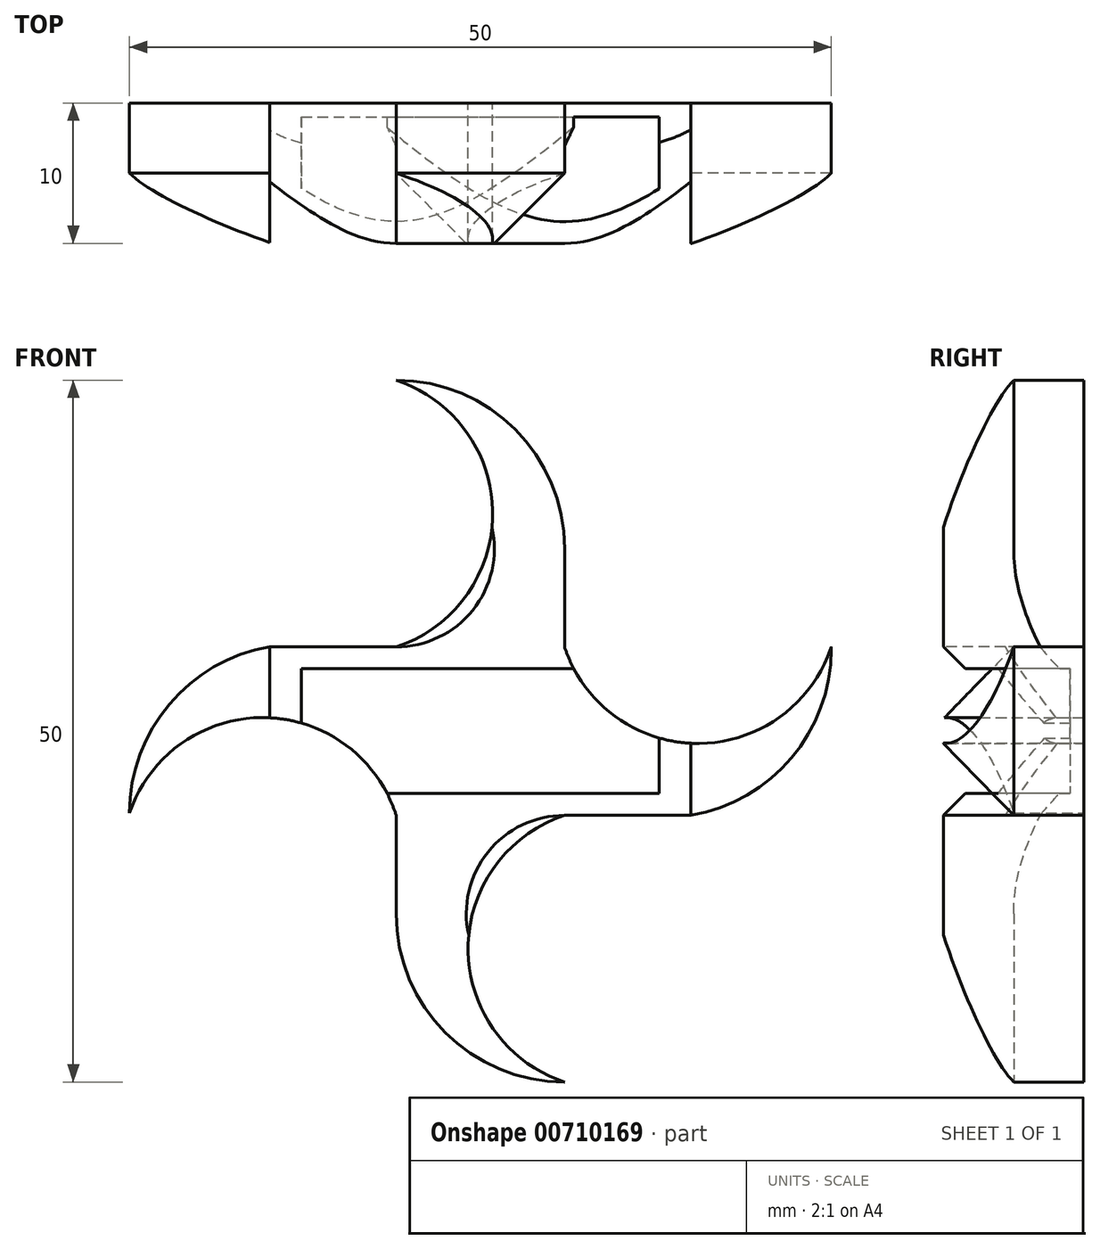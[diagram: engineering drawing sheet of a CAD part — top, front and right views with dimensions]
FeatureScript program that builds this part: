
annotation { "Feature Type Name" : "Feature", "Feature Type Description" : "" }
export const myFeature = defineFeature(function(context is Context, id is Id, definition is map)
    precondition{}
    {
        {
            var Q0;
            Q0=qCreatedBy(makeId("Top.planeOp"),FACE);
            var sketch = newSketch(context, id + "F0", { "sketchPlane" : qUnion([Q0])});
            skLineSegment(sketch, "E0", {"start": v(0, 0) * mm, "end": v(25.5, 0) * mm});
            skLineSegment(sketch, "E1", {"start": v(25.5, 0) * mm, "end": v(25.5, 8.9) * mm});
            skLineSegment(sketch, "E2", {"start": v(25.5, 8.9) * mm, "end": v(0, 8.9) * mm});
            skLineSegment(sketch, "E3", {"start": v(0, 8.9) * mm, "end": v(0, 0) * mm});
            skSolve(sketch);
        }
        {
            var Q0;
            Q0=makeQuery(id+"F0.imprint","IMPRINT",FACE,{"disambiguationData":[TD([[makeQuery(id+"F0.imprint","IMPRINT",EDGE,{"derivedFrom":sQuery(id+"F0.wireOp",EDGE,"E0")}),1.0]])]});
            extrude(context, id + "F1", {"entities" : qUnion([Q0]), "depth" : 8.9 * mm, "offsetDistance" : 25 * mm});
        }
        {
            var Q0;
            Q0=makeQuery(id+"F1.opExtrude","SWEPT_FACE",FACE,{"disambiguationData":[OSD([sQuery(id+"F0.wireOp",EDGE,"E0")])]});
            var sketch = newSketch(context, id + "F2", { "sketchPlane" : qUnion([Q0])});
            skLineSegment(sketch, "E4.bottom", {"start": v(-2.25, 10.45) * mm, "end": v(27.75, 10.45) * mm});
            skLineSegment(sketch, "E4.top", {"start": v(-2.25, -1.55) * mm, "end": v(27.75, -1.55) * mm});
            skLineSegment(sketch, "E4.left", {"start": v(-2.25, 10.45) * mm, "end": v(-2.25, -1.55) * mm});
            skLineSegment(sketch, "E4.right", {"start": v(27.75, 10.45) * mm, "end": v(27.75, -1.55) * mm});
            skPoint(sketch, "E4.middle", {"position": v(12.75, 4.45) * mm});
            skSolve(sketch);
        }
        {
            var Q0;
            {var subQ0=sQuery(id+"F0.wireOp",EDGE,"E0");Q0=makeQuery(id+"F2.imprint","IMPRINT",FACE,{"disambiguationData":[TD([[makeQuery(id+"F2.imprint","IMPRINT",EDGE,{"derivedFrom":makeQuery(id+"F1.opExtrude","CAP_EDGE",EDGE,{"disambiguationData":[OSD([subQ0])],"isStart":true})}),1.0]])]});}
            var Q1;
            Q1=makeQuery(id+"F2.imprint","IMPRINT",FACE,{"disambiguationData":[TD([[makeQuery(id+"F2.imprint","IMPRINT",EDGE,{"derivedFrom":sQuery(id+"F2.wireOp",EDGE,"E4.bottom")}),-1.0]])]});
            extrude(context, id + "F3", {"entities" : qUnion([Q0, Q1]), "oppositeDirection" : true, "depth" : 10 * mm, "offsetDistance" : 25 * mm});
        }
        {
            var Q0;
            Q0=makeQuery(id+"F1.opExtrude","SWEPT_FACE",FACE,{"disambiguationData":[OSD([sQuery(id+"F0.wireOp",EDGE,"E0")])]});
            extrude(context, id + "F4", {"entities" : qUnion([Q0]), "operationType" : NewBodyOperationType.REMOVE, "oppositeDirection" : true, "depth" : 9 * mm, "offsetDistance" : 25 * mm});
        }
        {
            var Q0;
            Q0=makeQuery(id+"F3.opExtrude","SWEPT_FACE",FACE,{"disambiguationData":[OSD([sQuery(id+"F2.wireOp",EDGE,"E4.left")])]});
            extrude(context, id + "F5", {"entities" : qUnion([Q0]), "depth" : 10 * mm, "offsetDistance" : 25 * mm});
        }
        {
            var Q0;
            Q0=makeQuery(id+"F3.opExtrude","SWEPT_FACE",FACE,{"disambiguationData":[OSD([sQuery(id+"F2.wireOp",EDGE,"E4.right")])]});
            extrude(context, id + "F6", {"entities" : qUnion([Q0]), "depth" : 10 * mm, "offsetDistance" : 25 * mm});
        }
        {
            var Q0;
            Q0=makeQuery(id+"F3.opExtrude","SWEPT_FACE",FACE,{"disambiguationData":[OSD([sQuery(id+"F2.wireOp",EDGE,"E4.bottom")])]});
            var sketch = newSketch(context, id + "F7", { "sketchPlane" : qUnion([Q0])});
            skLineSegment(sketch, "E5", {"start": v(12.75, 0) * mm, "end": v(18.75, 0) * mm});
            skLineSegment(sketch, "E6", {"start": v(18.75, 0) * mm, "end": v(18.75, 10) * mm});
            skLineSegment(sketch, "E7", {"start": v(18.75, 10) * mm, "end": v(12.75, 10) * mm});
            skLineSegment(sketch, "E8", {"start": v(12.75, 10) * mm, "end": v(6.75, 10) * mm});
            skLineSegment(sketch, "E9", {"start": v(6.75, 10) * mm, "end": v(6.75, 0) * mm});
            skLineSegment(sketch, "E10", {"start": v(12.75, 0) * mm, "end": v(6.75, 0) * mm});
            skSolve(sketch);
        }
        {
            var Q0;
            Q0=makeQuery(id+"F7.imprint","IMPRINT",FACE,{"disambiguationData":[TD([[makeQuery(id+"F7.imprint","IMPRINT",EDGE,{"derivedFrom":sQuery(id+"F7.wireOp",EDGE,"E5")}),1.0]])]});
            extrude(context, id + "F8", {"entities" : qUnion([Q0]), "operationType" : NewBodyOperationType.ADD, "depth" : 19 * mm, "offsetDistance" : 25 * mm});
        }
        {
            var Q0;
            Q0=makeQuery(id+"F3.opExtrude","SWEPT_FACE",FACE,{"disambiguationData":[OSD([sQuery(id+"F2.wireOp",EDGE,"E4.top")])]});
            var sketch = newSketch(context, id + "F9", { "sketchPlane" : qUnion([Q0])});
            skLineSegment(sketch, "E11", {"start": v(12.75, -10) * mm, "end": v(18.75, -10) * mm});
            skLineSegment(sketch, "E12", {"start": v(18.75, -10) * mm, "end": v(18.75, 0) * mm});
            skLineSegment(sketch, "E13", {"start": v(12.75, 0) * mm, "end": v(18.75, 0) * mm});
            skLineSegment(sketch, "E14", {"start": v(12.75, 0) * mm, "end": v(6.75, 0) * mm});
            skLineSegment(sketch, "E15", {"start": v(6.75, 0) * mm, "end": v(6.75, -10) * mm});
            skLineSegment(sketch, "E16", {"start": v(6.75, -10) * mm, "end": v(12.75, -10) * mm});
            skSolve(sketch);
        }
        {
            var Q0;
            Q0=makeQuery(id+"F9.imprint","IMPRINT",FACE,{"disambiguationData":[TD([[makeQuery(id+"F9.imprint","IMPRINT",EDGE,{"derivedFrom":sQuery(id+"F9.wireOp",EDGE,"E11")}),1.0]])]});
            extrude(context, id + "F10", {"entities" : qUnion([Q0]), "operationType" : NewBodyOperationType.ADD, "depth" : 19 * mm, "offsetDistance" : 25 * mm});
        }
        {
            var Q0;
            Q0=makeQuery(id+"F10.opExtrude","CAP_EDGE",EDGE,{"disambiguationData":[OSD([sQuery(id+"F9.wireOp",EDGE,"E15")])],"isStart":false});
            var Q1;
            Q1=makeQuery(id+"F5.opExtrude","CAP_EDGE",EDGE,{"disambiguationData":[OSD([sQuery(id+"F2.wireOp",EDGE,"E4.bottom"),sQuery(id+"F2.wireOp",EDGE,"E4.left")])],"isStart":false});
            var Q2;
            Q2=makeQuery(id+"F8.opExtrude","CAP_EDGE",EDGE,{"disambiguationData":[OSD([sQuery(id+"F7.wireOp",EDGE,"E6")])],"isStart":false});
            var Q3;
            Q3=makeQuery(id+"F6.opExtrude","CAP_EDGE",EDGE,{"disambiguationData":[OSD([sQuery(id+"F2.wireOp",EDGE,"E4.top"),sQuery(id+"F2.wireOp",EDGE,"E4.right")])],"isStart":false});
            fillet(context, id + "F11", {"entities" : qUnion([Q0, Q1, Q2, Q3]), "radius" : 12 * mm, "tangentPropagation" : true, "allowEdgeOverflow" : false});
        }
        {
            var Q0;
            Q0=makeQuery(id+"F10.boolean.opBoolean","MERGE",FACE,{"derivedFrom":[makeQuery(id+"F8.boolean.opBoolean","MERGE",FACE,{"derivedFrom":[makeQuery(id+"F3.opExtrude","CAP_FACE",FACE,{"disambiguationData":[OSD([sQuery(id+"F2.wireOp",EDGE,"E4.bottom"),sQuery(id+"F2.wireOp",EDGE,"E4.top"),sQuery(id+"F2.wireOp",EDGE,"E4.left"),sQuery(id+"F2.wireOp",EDGE,"E4.right")])],"isStart":false}),makeQuery(id+"F8.opExtrude","SWEPT_FACE",FACE,{"disambiguationData":[OSD([sQuery(id+"F7.wireOp",EDGE,"E7"),sQuery(id+"F7.wireOp",EDGE,"E8")])]})]}),makeQuery(id+"F10.opExtrude","SWEPT_FACE",FACE,{"disambiguationData":[OSD([sQuery(id+"F9.wireOp",EDGE,"E11"),sQuery(id+"F9.wireOp",EDGE,"E16")])]})]});
            var sketch = newSketch(context, id + "F12", { "sketchPlane" : qUnion([Q0])});
            skPoint(sketch, "E17.0", {"position": v(-12.75, 10.45) * mm});
            skLineSegment(sketch, "E18", {"start": v(-18.75, 10.45) * mm, "end": v(-18.75, -1.55) * mm});
            skLineSegment(sketch, "E19", {"start": v(-18.75, -1.55) * mm, "end": v(-6.75, -1.55) * mm});
            skLineSegment(sketch, "E20", {"start": v(-6.75, -1.55) * mm, "end": v(-6.75, 10.45) * mm});
            skLineSegment(sketch, "E21", {"start": v(-6.75, 10.45) * mm, "end": v(-18.75, 10.45) * mm});
            skLineSegment(sketch, "E22.0.0", {"start": v(12.25, -1.55) * mm, "end": v(12.25, -1.38) * mm});
            skArc(sketch, "E22.0.1", {"start": v(12.25, -1.38) * mm, "mid": v(9.42, 6.36) * mm, "end": v(2.25, 10.45) * mm});
            skLineSegment(sketch, "E22.0.2", {"start": v(2.25, 10.45) * mm, "end": v(2.25, -1.55) * mm});
            skLineSegment(sketch, "E22.0.3", {"start": v(2.25, -1.55) * mm, "end": v(12.25, -1.55) * mm});
            skLineSegment(sketch, "E23.0.0", {"start": v(-37.75, 10.45) * mm, "end": v(-37.75, 10.28) * mm});
            skArc(sketch, "E23.0.1", {"start": v(-37.75, 10.28) * mm, "mid": v(-34.92, 2.54) * mm, "end": v(-27.75, -1.55) * mm});
            skLineSegment(sketch, "E23.0.2", {"start": v(-27.75, -1.55) * mm, "end": v(-27.75, 10.45) * mm});
            skLineSegment(sketch, "E23.0.3", {"start": v(-27.75, 10.45) * mm, "end": v(-37.75, 10.45) * mm});
            skLineSegment(sketch, "E24.0.0", {"start": v(-18.75, -1.55) * mm, "end": v(-18.75, -20.55) * mm});
            skArc(sketch, "E24.0.1", {"start": v(-18.75, -20.55) * mm, "mid": v(-10.26, -17.04) * mm, "end": v(-6.75, -8.55) * mm});
            skLineSegment(sketch, "E24.0.2", {"start": v(-6.75, -8.55) * mm, "end": v(-6.75, -1.55) * mm});
            skLineSegment(sketch, "E24.0.3", {"start": v(-6.75, -1.55) * mm, "end": v(2.25, -1.55) * mm});
            skLineSegment(sketch, "E24.0.4", {"start": v(2.25, -1.55) * mm, "end": v(2.25, 10.45) * mm});
            skLineSegment(sketch, "E24.0.5", {"start": v(2.25, 10.45) * mm, "end": v(-6.75, 10.45) * mm});
            skLineSegment(sketch, "E24.0.6", {"start": v(-6.75, 10.45) * mm, "end": v(-6.75, 29.45) * mm});
            skArc(sketch, "E24.0.7", {"start": v(-6.75, 29.45) * mm, "mid": v(-15.24, 25.94) * mm, "end": v(-18.75, 17.45) * mm});
            skLineSegment(sketch, "E24.0.8", {"start": v(-18.75, 17.45) * mm, "end": v(-18.75, 10.45) * mm});
            skLineSegment(sketch, "E24.0.9", {"start": v(-18.75, 10.45) * mm, "end": v(-27.75, 10.45) * mm});
            skLineSegment(sketch, "E24.0.10", {"start": v(-27.75, 10.45) * mm, "end": v(-27.75, -1.55) * mm});
            skLineSegment(sketch, "E24.0.11", {"start": v(-27.75, -1.55) * mm, "end": v(-18.75, -1.55) * mm});
            skArc(sketch, "E25", {"start": v(-6.75, 29.45) * mm, "mid": v(-13.63, 19.95) * mm, "end": v(-6.75, 10.45) * mm});
            skArc(sketch, "E26", {"start": v(12.25, -1.38) * mm, "mid": v(2.69, 5.41) * mm, "end": v(-6.75, -1.55) * mm});
            skArc(sketch, "E27", {"start": v(-18.75, -20.55) * mm, "mid": v(-11.87, -11.05) * mm, "end": v(-18.75, -1.55) * mm});
            skArc(sketch, "E28", {"start": v(-37.75, 10.45) * mm, "mid": v(-28.25, 3.57) * mm, "end": v(-18.75, 10.45) * mm});
            skSolve(sketch);
        }
        {
            var Q0;
            {var subQ0=sQuery(id+"F12.wireOp",EDGE,"E23.0.3");Q0=makeQuery(id+"F12.imprint","IMPRINT",FACE,{"disambiguationData":[TD([[makeQuery(id+"F12.imprint","IMPRINT",EDGE,{"derivedFrom":subQ0}),1.0]])]});}
            var Q1;
            {var subQ0=sQuery(id+"F12.wireOp",EDGE,"E24.0.9");Q1=makeQuery(id+"F12.imprint","IMPRINT",FACE,{"disambiguationData":[TD([[makeQuery(id+"F12.imprint","IMPRINT",EDGE,{"derivedFrom":subQ0}),1.0]])]});}
            var Q2;
            Q2=makeQuery(id+"F12.imprint","IMPRINT",FACE,{"disambiguationData":[TD([[makeQuery(id+"F12.imprint","IMPRINT",EDGE,{"derivedFrom":sQuery(id+"F12.wireOp",EDGE,"E24.0.6")}),-1.0]])]});
            var Q3;
            {var subQ0=sQuery(id+"F12.wireOp",EDGE,"E22.0.0");Q3=makeQuery(id+"F12.imprint","IMPRINT",FACE,{"disambiguationData":[TD([[makeQuery(id+"F12.imprint","IMPRINT",EDGE,{"derivedFrom":subQ0}),1.0]])]});}
            var Q4;
            {var subQ0=sQuery(id+"F12.wireOp",EDGE,"E24.0.3");Q4=makeQuery(id+"F12.imprint","IMPRINT",FACE,{"disambiguationData":[TD([[makeQuery(id+"F12.imprint","IMPRINT",EDGE,{"derivedFrom":subQ0}),-1.0]])]});}
            var Q5;
            Q5=makeQuery(id+"F12.imprint","IMPRINT",FACE,{"disambiguationData":[TD([[makeQuery(id+"F12.imprint","IMPRINT",EDGE,{"derivedFrom":sQuery(id+"F12.wireOp",EDGE,"E24.0.0")}),-1.0]])]});
            extrude(context, id + "F13", {"entities" : qUnion([Q0, Q1, Q2, Q3, Q4, Q5]), "operationType" : NewBodyOperationType.REMOVE, "oppositeDirection" : true, "depth" : 10 * mm, "offsetDistance" : 25 * mm});
        }
        {
            var Q0;
            {var subQ0=sQuery(id+"F2.wireOp",EDGE,"E4.right");Q0=makeQuery(id+"F11.opFillet","BLEND_EDGE",EDGE,{"blendedFrom":[makeQuery(id+"F6.opExtrude","CAP_EDGE",EDGE,{"disambiguationData":[OSD([sQuery(id+"F2.wireOp",EDGE,"E4.top"),subQ0])],"isStart":false}),makeQuery(id+"F6.opExtrude","SWEPT_FACE",FACE,{"disambiguationData":[OSD([subQ0]),TDD([makeQuery(id+"F3.opExtrude","CAP_EDGE",EDGE,{"disambiguationData":[OSD([subQ0])],"isStart":true})])]})],"blendedInto":[makeQuery(id+"F6.opExtrude","SWEPT_FACE",FACE,{"disambiguationData":[OSD([subQ0]),TDD([makeQuery(id+"F3.opExtrude","CAP_EDGE",EDGE,{"disambiguationData":[OSD([subQ0])],"isStart":true})])]})]});}
            var Q1;
            Q1=makeQuery(id+"F11.opFillet","BLEND_EDGE",EDGE,{"blendedFrom":[makeQuery(id+"F10.opExtrude","CAP_EDGE",EDGE,{"disambiguationData":[OSD([sQuery(id+"F9.wireOp",EDGE,"E15")])],"isStart":false}),makeQuery(id+"F10.boolean.opBoolean","MERGE",FACE,{"derivedFrom":[makeQuery(id+"F8.boolean.opBoolean","MERGE",FACE,{"derivedFrom":[makeQuery(id+"F3.opExtrude","CAP_FACE",FACE,{"disambiguationData":[OSD([sQuery(id+"F2.wireOp",EDGE,"E4.bottom"),sQuery(id+"F2.wireOp",EDGE,"E4.top"),sQuery(id+"F2.wireOp",EDGE,"E4.left"),sQuery(id+"F2.wireOp",EDGE,"E4.right")])],"isStart":true}),makeQuery(id+"F8.opExtrude","SWEPT_FACE",FACE,{"disambiguationData":[OSD([sQuery(id+"F7.wireOp",EDGE,"E5"),sQuery(id+"F7.wireOp",EDGE,"E10")])]})]}),makeQuery(id+"F10.opExtrude","SWEPT_FACE",FACE,{"disambiguationData":[OSD([sQuery(id+"F9.wireOp",EDGE,"E13"),sQuery(id+"F9.wireOp",EDGE,"E14")])]})]})],"blendedInto":[makeQuery(id+"F10.boolean.opBoolean","MERGE",FACE,{"derivedFrom":[makeQuery(id+"F8.boolean.opBoolean","MERGE",FACE,{"derivedFrom":[makeQuery(id+"F3.opExtrude","CAP_FACE",FACE,{"disambiguationData":[OSD([sQuery(id+"F2.wireOp",EDGE,"E4.bottom"),sQuery(id+"F2.wireOp",EDGE,"E4.top"),sQuery(id+"F2.wireOp",EDGE,"E4.left"),sQuery(id+"F2.wireOp",EDGE,"E4.right")])],"isStart":true}),makeQuery(id+"F8.opExtrude","SWEPT_FACE",FACE,{"disambiguationData":[OSD([sQuery(id+"F7.wireOp",EDGE,"E5"),sQuery(id+"F7.wireOp",EDGE,"E10")])]})]}),makeQuery(id+"F10.opExtrude","SWEPT_FACE",FACE,{"disambiguationData":[OSD([sQuery(id+"F9.wireOp",EDGE,"E13"),sQuery(id+"F9.wireOp",EDGE,"E14")])]})]})]});
            var Q2;
            {var subQ0=sQuery(id+"F2.wireOp",EDGE,"E4.left");Q2=makeQuery(id+"F11.opFillet","BLEND_EDGE",EDGE,{"blendedFrom":[makeQuery(id+"F5.opExtrude","CAP_EDGE",EDGE,{"disambiguationData":[OSD([sQuery(id+"F2.wireOp",EDGE,"E4.bottom"),subQ0])],"isStart":false}),makeQuery(id+"F5.opExtrude","SWEPT_FACE",FACE,{"disambiguationData":[OSD([subQ0]),TDD([makeQuery(id+"F3.opExtrude","CAP_EDGE",EDGE,{"disambiguationData":[OSD([subQ0])],"isStart":true})])]})],"blendedInto":[makeQuery(id+"F5.opExtrude","SWEPT_FACE",FACE,{"disambiguationData":[OSD([subQ0]),TDD([makeQuery(id+"F3.opExtrude","CAP_EDGE",EDGE,{"disambiguationData":[OSD([subQ0])],"isStart":true})])]})]});}
            var Q3;
            Q3=makeQuery(id+"F11.opFillet","BLEND_EDGE",EDGE,{"blendedFrom":[makeQuery(id+"F8.opExtrude","CAP_EDGE",EDGE,{"disambiguationData":[OSD([sQuery(id+"F7.wireOp",EDGE,"E6")])],"isStart":false}),makeQuery(id+"F10.boolean.opBoolean","MERGE",FACE,{"derivedFrom":[makeQuery(id+"F8.boolean.opBoolean","MERGE",FACE,{"derivedFrom":[makeQuery(id+"F3.opExtrude","CAP_FACE",FACE,{"disambiguationData":[OSD([sQuery(id+"F2.wireOp",EDGE,"E4.bottom"),sQuery(id+"F2.wireOp",EDGE,"E4.top"),sQuery(id+"F2.wireOp",EDGE,"E4.left"),sQuery(id+"F2.wireOp",EDGE,"E4.right")])],"isStart":true}),makeQuery(id+"F8.opExtrude","SWEPT_FACE",FACE,{"disambiguationData":[OSD([sQuery(id+"F7.wireOp",EDGE,"E5"),sQuery(id+"F7.wireOp",EDGE,"E10")])]})]}),makeQuery(id+"F10.opExtrude","SWEPT_FACE",FACE,{"disambiguationData":[OSD([sQuery(id+"F9.wireOp",EDGE,"E13"),sQuery(id+"F9.wireOp",EDGE,"E14")])]})]})],"blendedInto":[makeQuery(id+"F10.boolean.opBoolean","MERGE",FACE,{"derivedFrom":[makeQuery(id+"F8.boolean.opBoolean","MERGE",FACE,{"derivedFrom":[makeQuery(id+"F3.opExtrude","CAP_FACE",FACE,{"disambiguationData":[OSD([sQuery(id+"F2.wireOp",EDGE,"E4.bottom"),sQuery(id+"F2.wireOp",EDGE,"E4.top"),sQuery(id+"F2.wireOp",EDGE,"E4.left"),sQuery(id+"F2.wireOp",EDGE,"E4.right")])],"isStart":true}),makeQuery(id+"F8.opExtrude","SWEPT_FACE",FACE,{"disambiguationData":[OSD([sQuery(id+"F7.wireOp",EDGE,"E5"),sQuery(id+"F7.wireOp",EDGE,"E10")])]})]}),makeQuery(id+"F10.opExtrude","SWEPT_FACE",FACE,{"disambiguationData":[OSD([sQuery(id+"F9.wireOp",EDGE,"E13"),sQuery(id+"F9.wireOp",EDGE,"E14")])]})]})]});
            chamfer(context, id + "F14", {"entities" : qUnion([Q0, Q1, Q2, Q3]), "width" : 5 * mm, "tangentPropagation" : true});
        }
    });
